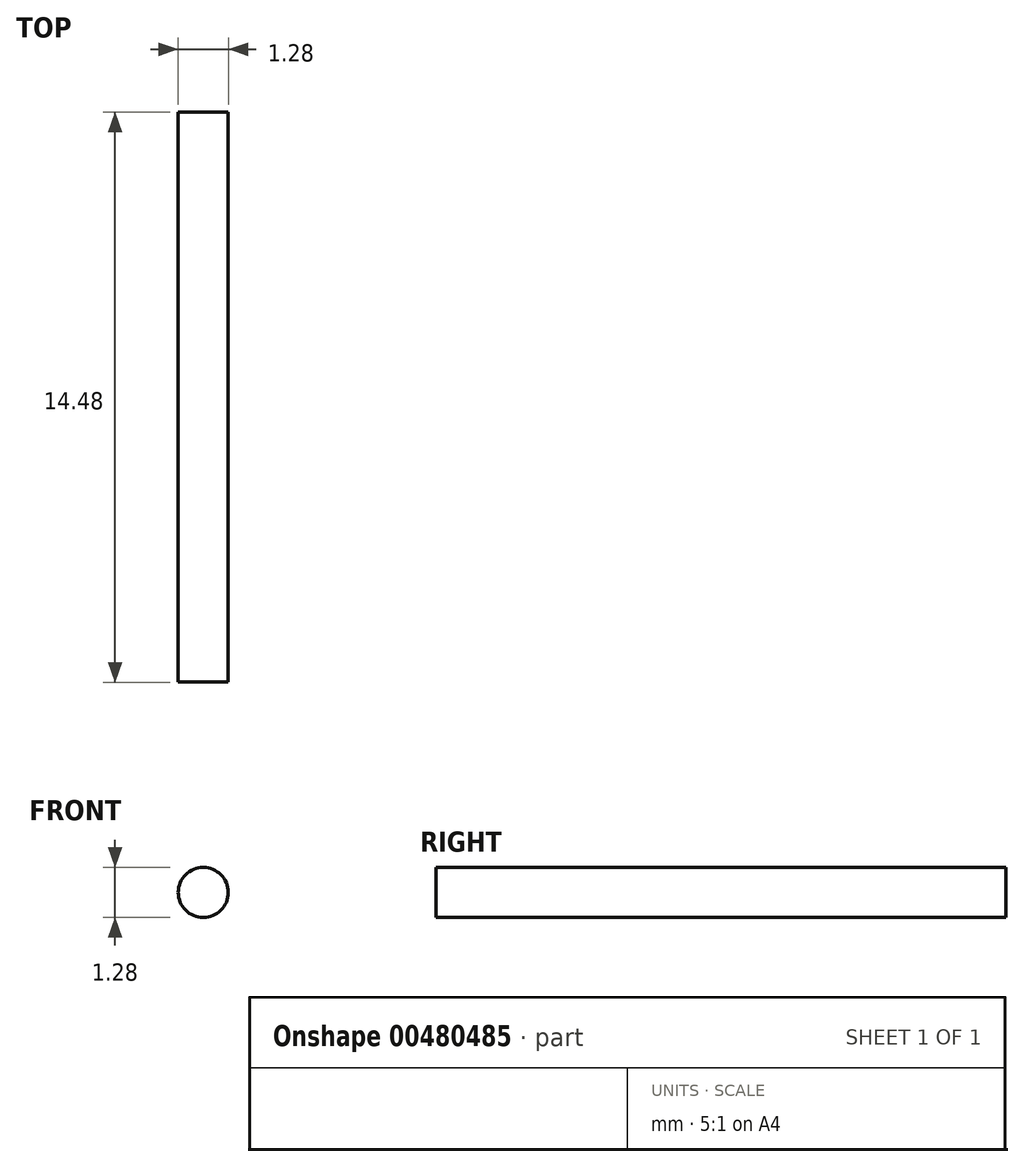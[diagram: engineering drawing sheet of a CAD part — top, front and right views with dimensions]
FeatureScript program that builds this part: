
annotation { "Feature Type Name" : "Feature", "Feature Type Description" : "" }
export const myFeature = defineFeature(function(context is Context, id is Id, definition is map)
    precondition{}
    {
        {
            var Q0;
            Q0=qCreatedBy(makeId("Front.planeOp"),FACE);
            var sketch = newSketch(context, id + "F0", { "sketchPlane" : qUnion([Q0])});
            skCircle(sketch, "E0", {"center": v(0, 0) * mm, "radius": 0.64 * mm});
            skSolve(sketch);
        }
        {
            var Q0;
            Q0 = qSketchRegion(id + "F0", true);
            extrude(context, id + "F1", {"entities" : qUnion([Q0]), "depth" : 14.48 * mm});
        }
    });
